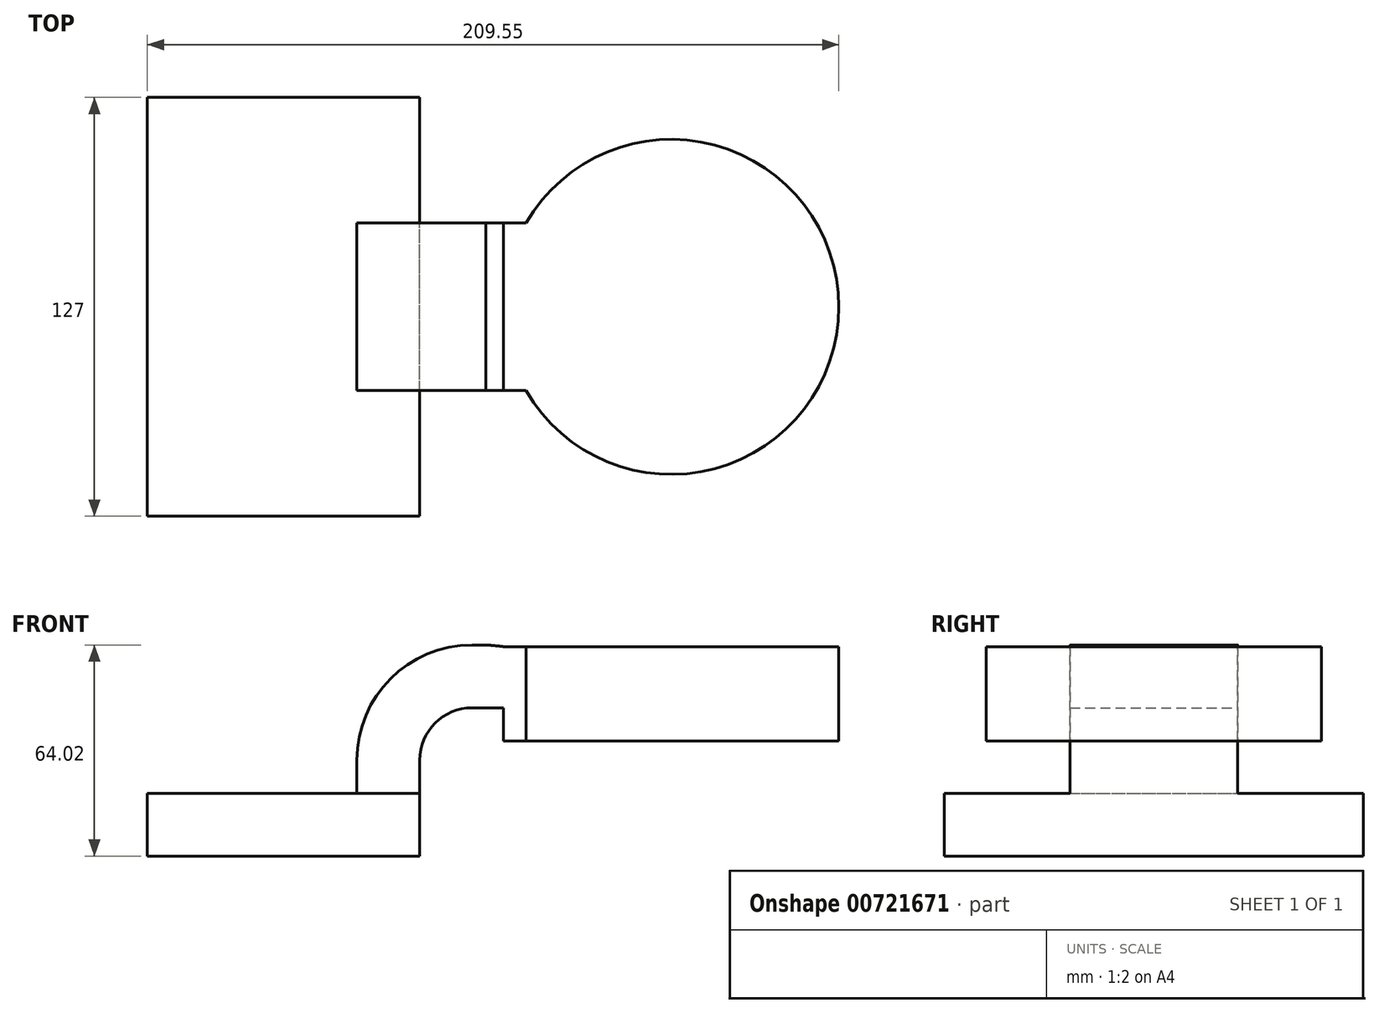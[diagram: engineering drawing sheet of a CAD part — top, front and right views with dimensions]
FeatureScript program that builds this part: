
annotation { "Feature Type Name" : "Feature", "Feature Type Description" : "" }
export const myFeature = defineFeature(function(context is Context, id is Id, definition is map)
    precondition{}
    {
        {
            var Q0;
            Q0=qCreatedBy(makeId("Front.planeOp"),FACE);
            var sketch = newSketch(context, id + "F0", { "sketchPlane" : qUnion([Q0])});
            skLineSegment(sketch, "E0.bottom", {"start": v(-41.28, 9.52) * mm, "end": v(41.27, 9.53) * mm});
            skLineSegment(sketch, "E0.top", {"start": v(-41.28, -9.53) * mm, "end": v(41.28, -9.53) * mm});
            skLineSegment(sketch, "E0.left", {"start": v(-41.28, 9.52) * mm, "end": v(-41.28, -9.53) * mm});
            skLineSegment(sketch, "E0.right", {"start": v(41.27, 9.53) * mm, "end": v(41.28, -9.52) * mm});
            skPoint(sketch, "E0.middle", {"position": v(0, 0) * mm});
            skLineSegment(sketch, "E1.bottom", {"start": v(66.67, 53.98) * mm, "end": v(117.48, 53.98) * mm});
            skLineSegment(sketch, "E1.top", {"start": v(66.67, 25.4) * mm, "end": v(117.48, 25.4) * mm});
            skLineSegment(sketch, "E1.left", {"start": v(66.67, 53.98) * mm, "end": v(66.67, 25.4) * mm});
            skLineSegment(sketch, "E1.right", {"start": v(117.48, 53.98) * mm, "end": v(117.48, 25.4) * mm});
            skPoint(sketch, "E1.middle", {"position": v(92.08, 39.69) * mm});
            skLineSegment(sketch, "E2", {"start": v(41.27, 9.53) * mm, "end": v(41.27, 19.56) * mm});
            skArc(sketch, "E3", {"start": v(41.27, 19.56) * mm, "mid": v(45.92, 30.79) * mm, "end": v(57.15, 35.44) * mm});
            skLineSegment(sketch, "E4", {"start": v(57.15, 35.44) * mm, "end": v(77.87, 35.44) * mm});
            skLineSegment(sketch, "E5.0", {"start": v(57.15, 54.49) * mm, "end": v(77.87, 54.49) * mm});
            skArc(sketch, "E5.1", {"start": v(22.22, 19.56) * mm, "mid": v(32.45, 44.26) * mm, "end": v(57.15, 54.49) * mm});
            skLineSegment(sketch, "E5.2", {"start": v(22.22, 9.53) * mm, "end": v(22.22, 19.56) * mm});
            skFitSpline(sketch, "E6", {"points": [v(-41.28, 9.52) * mm, v(66.68, 53.98) * mm], "startDerivative": vector(74.73, 128.49) * mm, "endDerivative": vector(132.56, -14) * mm});
            skSolve(sketch);
        }
        {
            var Q0;
            Q0=makeQuery(id+"F0.imprint","IMPRINT",FACE,{"disambiguationData":[TD([[makeQuery(id+"F0.imprint","IMPRINT",EDGE,{"derivedFrom":sQuery(id+"F0.wireOp",EDGE,"E0.top")}),1.0]])]});
            extrude(context, id + "F1", {"entities" : qUnion([Q0]), "endBound" : BoundingType.SYMMETRIC, "depth" : 127 * mm, "offsetDistance" : 25.4 * mm});
        }
        {
            var Q0;
            {var subQ0=sQuery(id+"F0.wireOp",EDGE,"E5.1");Q0=makeQuery(id+"F0.imprint","IMPRINT",FACE,{"disambiguationData":[TD([[makeQuery(id+"F0.imprint","IMPRINT",EDGE,{"derivedFrom":subQ0}),1.0]])]});}
            extrude(context, id + "F2", {"entities" : qUnion([Q0]), "operationType" : NewBodyOperationType.ADD, "endBound" : BoundingType.SYMMETRIC, "depth" : 15.88 * mm, "offsetDistance" : 25.4 * mm});
        }
        {
            var Q0;
            {var subQ0=sQuery(id+"F0.wireOp",EDGE,"E2");Q0=makeQuery(id+"F0.imprint","IMPRINT",FACE,{"disambiguationData":[TD([[makeQuery(id+"F0.imprint","IMPRINT",EDGE,{"derivedFrom":subQ0}),1.0]])]});}
            var Q1;
            {var subQ3=sQuery(id+"F0.wireOp",EDGE,"E1.bottom");Q1=makeQuery(id+"F0.imprint","IMPRINT",FACE,{"disambiguationData":[TD([[makeQuery(id+"F0.imprint","IMPRINT",EDGE,{"derivedFrom":subQ3}),-1.0]])]});}
            extrude(context, id + "F3", {"entities" : qUnion([Q0, Q1]), "operationType" : NewBodyOperationType.ADD, "endBound" : BoundingType.SYMMETRIC, "depth" : 50.8 * mm, "offsetDistance" : 25.4 * mm});
        }
        {
            var Q0;
            {var subQ3=sQuery(id+"F0.wireOp",EDGE,"E1.bottom");Q0=makeQuery(id+"F0.imprint","IMPRINT",FACE,{"disambiguationData":[TD([[makeQuery(id+"F0.imprint","IMPRINT",EDGE,{"derivedFrom":subQ3}),-1.0]])]});}
            var Q1;
            Q1=sQuery(id+"F0.wireOp",EDGE,"E1.right");
            revolve(context, id + "F4", {"operationType" : NewBodyOperationType.ADD, "surfaceOperationType" : NewSurfaceOperationType.NEW, "entities" : qUnion([Q0]), "axis" : qUnion([Q1]), "revolveType" : RevolveType.FULL});
        }
    });
